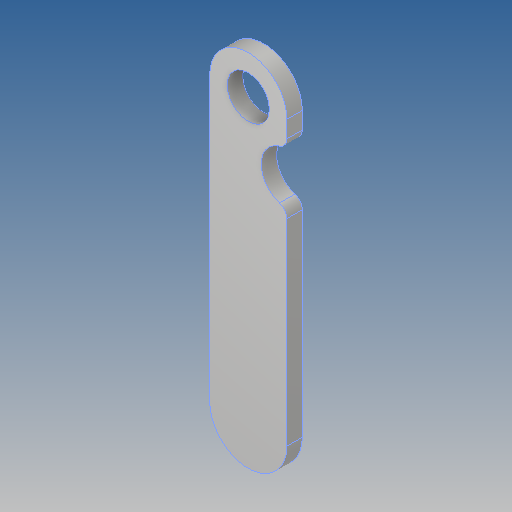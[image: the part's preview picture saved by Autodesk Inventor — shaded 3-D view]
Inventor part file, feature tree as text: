
AUTODESK INVENTOR PART (.ipt)
format: ipt  version: 2018 (Build 220112000, 112)  size: 113,152 bytes
history: native  units: mm
features: extrude x1, fillet x1, sketch x1
ambient origin geometry x8: Origin, YZ Plane, XZ Plane, XY Plane, X Axis, Y Axis, Z Axis, Center Point
bodies: Solid1 (feature_tree)
feature tree (3):
  extrude  "Extrusion1"  Depth=15.0mm
  fillet  "Fillet1"  Radius=8.2mm
  sketch  "Sketch1"  dims[d0=55.0mm d1=15.0mm d2=8.2mm d3=8.2mm d4=10.0mm d5=10.0mm d6=3.0mm d7=0.0mm d8=15.0mm d10=15.0mm d11=2.0mm]
